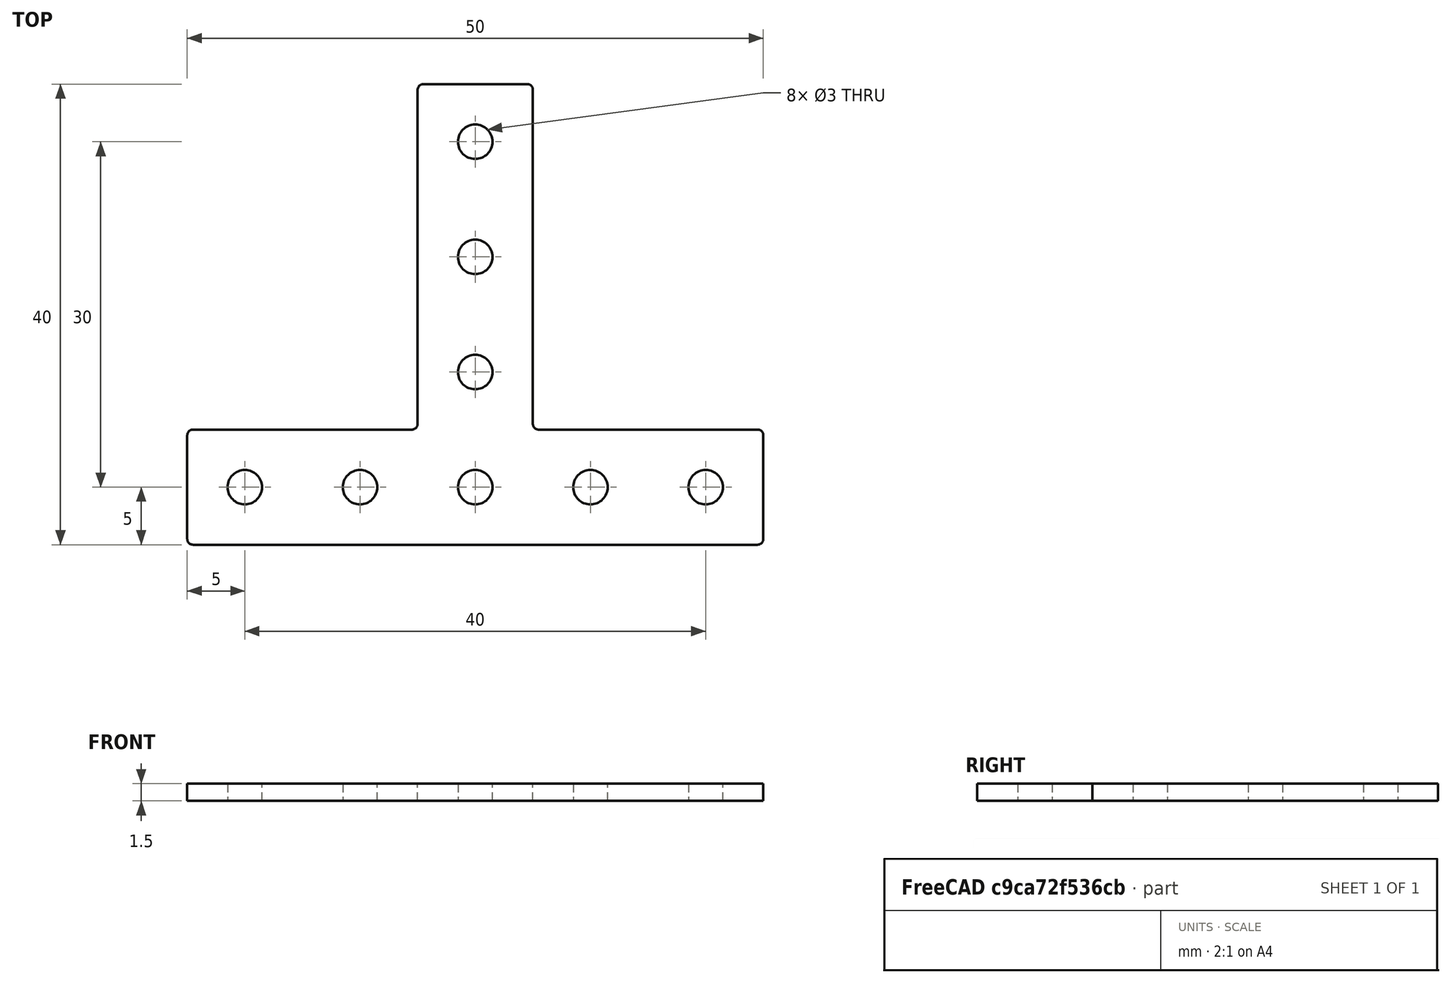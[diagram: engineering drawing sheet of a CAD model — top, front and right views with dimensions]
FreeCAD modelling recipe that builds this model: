
FCSTD DOCUMENT  (FreeCAD 0.18R16146 (Git))
Label: makerbeam_bracket_T
License: All rights reserved
LicenseURL: http://en.wikipedia.org/wiki/All_rights_reserved
objects: Sketcher::SketchObject×1, PartDesign::Pad×1, PartDesign::Fillet×1, PartDesign::Body×1
note: 5 computed .brp shape members not serialized (recipe doc carries the construction recipe); baked Part::Feature solids carry a one-line shape summary decoded from their .brp

FEATURE [Sketcher::SketchObject] Sketch
  MapMode = 5
  Support = -> [XY_Plane]
  sketch-geometry (16):
    g0: Circle CenterX=-20 CenterY=0 CenterZ=0 NormalX=0 NormalY=0 NormalZ=1 AngleXU=0 Radius=1.5
    g1: Circle CenterX=-10 CenterY=0 CenterZ=0 NormalX=0 NormalY=0 NormalZ=1 AngleXU=0 Radius=1.5
    g2: Circle CenterX=0 CenterY=0 CenterZ=0 NormalX=0 NormalY=0 NormalZ=1 AngleXU=0 Radius=1.5
    g3: Circle CenterX=10 CenterY=0 CenterZ=0 NormalX=0 NormalY=0 NormalZ=1 AngleXU=0 Radius=1.5
    g4: Circle CenterX=20 CenterY=0 CenterZ=0 NormalX=0 NormalY=0 NormalZ=1 AngleXU=0 Radius=1.5
    g5: LineSegment StartX=-25 StartY=5 StartZ=0 EndX=-5 EndY=5 EndZ=0
    g6: LineSegment StartX=25 StartY=5 StartZ=0 EndX=25 EndY=-5 EndZ=0
    g7: LineSegment StartX=25 StartY=-5 StartZ=0 EndX=-25 EndY=-5 EndZ=0
    g8: LineSegment StartX=-25 StartY=-5 StartZ=0 EndX=-25 EndY=5 EndZ=0
    g9: Circle CenterX=0 CenterY=10 CenterZ=0 NormalX=0 NormalY=0 NormalZ=1 AngleXU=0 Radius=1.5
    g10: Circle CenterX=0 CenterY=20 CenterZ=0 NormalX=0 NormalY=0 NormalZ=1 AngleXU=0 Radius=1.5
    g11: LineSegment StartX=-5 StartY=35 StartZ=0 EndX=5 EndY=35 EndZ=0
    g12: LineSegment StartX=5 StartY=35 StartZ=0 EndX=5 EndY=5 EndZ=0
    g13: LineSegment StartX=-5 StartY=5 StartZ=0 EndX=-5 EndY=35 EndZ=0
    g14: LineSegment StartX=5 StartY=5 StartZ=0 EndX=25 EndY=5 EndZ=0
    g15: Circle CenterX=0 CenterY=30 CenterZ=0 NormalX=0 NormalY=0 NormalZ=1 AngleXU=0 Radius=1.5
  constraints (25):
    c: Radius(g0) = 1.5
    c: Equal(g0,g1) = 1.5
    c: Equal(g0,g2) = 1.5
    c: Equal(g0,g3) = 1.5
    c: Equal(g0,g4) = 1.5
    c: Coincident(g14,g6)
    c: Coincident(g6,g7)
    c: Coincident(g7,g8)
    c: Coincident(g8,g5)
    c: Horizontal(g5)
    c: Horizontal(g7)
    c: Vertical(g6)
    c: Vertical(g8)
    c: DistanceX(g7,g7) = 50
    c: DistanceY(g6,g6) = 10
    c: PointOnObject(g9,g-2)
    c: PointOnObject(g10,g-2)
    c: Coincident(g11,g12)
    c: Coincident(g13,g11)
    c: Horizontal(g11)
    c: Vertical(g12)
    c: Vertical(g13)
    c: Tangent(g5,g14)
    c: Coincident(g13,g5)
    c: Coincident(g12,g14)
FEATURE [PartDesign::Pad] Pad
  Length = 1.5
  Length2 = 100
  Profile = -> Sketch
  Type = 0
FEATURE [PartDesign::Fillet] Fillet
  Base = -> Pad [Edge2,Edge5,Edge8,Edge1,Edge11,Edge14,Edge20,Edge17]
  BaseFeature = -> Pad
  Radius = 0.5
FEATURE [PartDesign::Body] Body  label="makerbeam_bracket_straight"
  Group = -> [Sketch,Pad,Fillet]
  Origin = -> Origin
  Tip = -> Fillet
